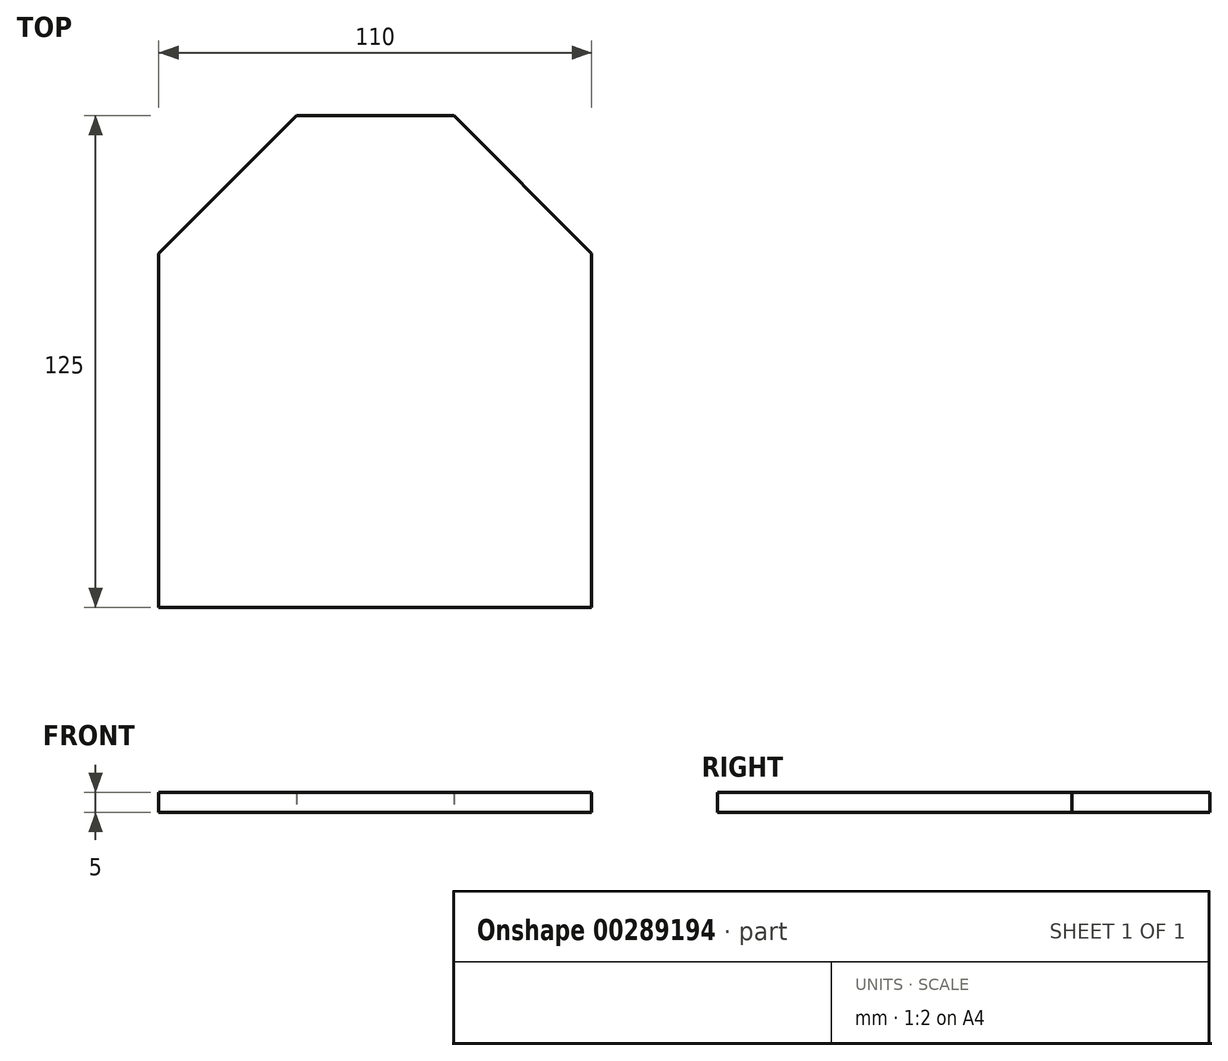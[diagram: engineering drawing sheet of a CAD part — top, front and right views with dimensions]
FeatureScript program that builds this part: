
annotation { "Feature Type Name" : "Feature", "Feature Type Description" : "" }
export const myFeature = defineFeature(function(context is Context, id is Id, definition is map)
    precondition{}
    {
        {
            var Q0;
            Q0=qCreatedBy(makeId("Top.planeOp"),FACE);
            var sketch = newSketch(context, id + "F0", { "sketchPlane" : qUnion([Q0])});
            skLineSegment(sketch, "E0", {"start": v(0, 62.5) * mm, "end": v(0, -62.5) * mm, "construction": true});
            skLineSegment(sketch, "E1", {"start": v(55, 0) * mm, "end": v(-55, 0) * mm, "construction": true});
            skLineSegment(sketch, "E2.bottom", {"start": v(-20, 62.5) * mm, "end": v(55, 62.5) * mm});
            skLineSegment(sketch, "E2.top", {"start": v(-55, -62.5) * mm, "end": v(55, -62.5) * mm});
            skLineSegment(sketch, "E2.left", {"start": v(-55, 27.5) * mm, "end": v(-55, -62.5) * mm});
            skLineSegment(sketch, "E2.right", {"start": v(55, 62.5) * mm, "end": v(55, -62.5) * mm});
            skLineSegment(sketch, "E3", {"start": v(-55, 27.5) * mm, "end": v(-20, 62.5) * mm});
            skLineSegment(sketch, "E4.MirrorCS", {"start": v(55, 27.5) * mm, "end": v(20, 62.5) * mm});
            skPoint(sketch, "E5.orphan", {"position": v(-55, 62.5) * mm});
            skSolve(sketch);
        }
        {
            var Q0;
            {var subQ0=sQuery(id+"F0.wireOp",EDGE,"E2.top");Q0=makeQuery(id+"F0.imprint","IMPRINT",FACE,{"disambiguationData":[TD([[makeQuery(id+"F0.imprint","IMPRINT",EDGE,{"derivedFrom":subQ0}),1.0]])]});}
            extrude(context, id + "F1", {"entities" : qUnion([Q0]), "depth" : 5 * mm});
        }
    });
